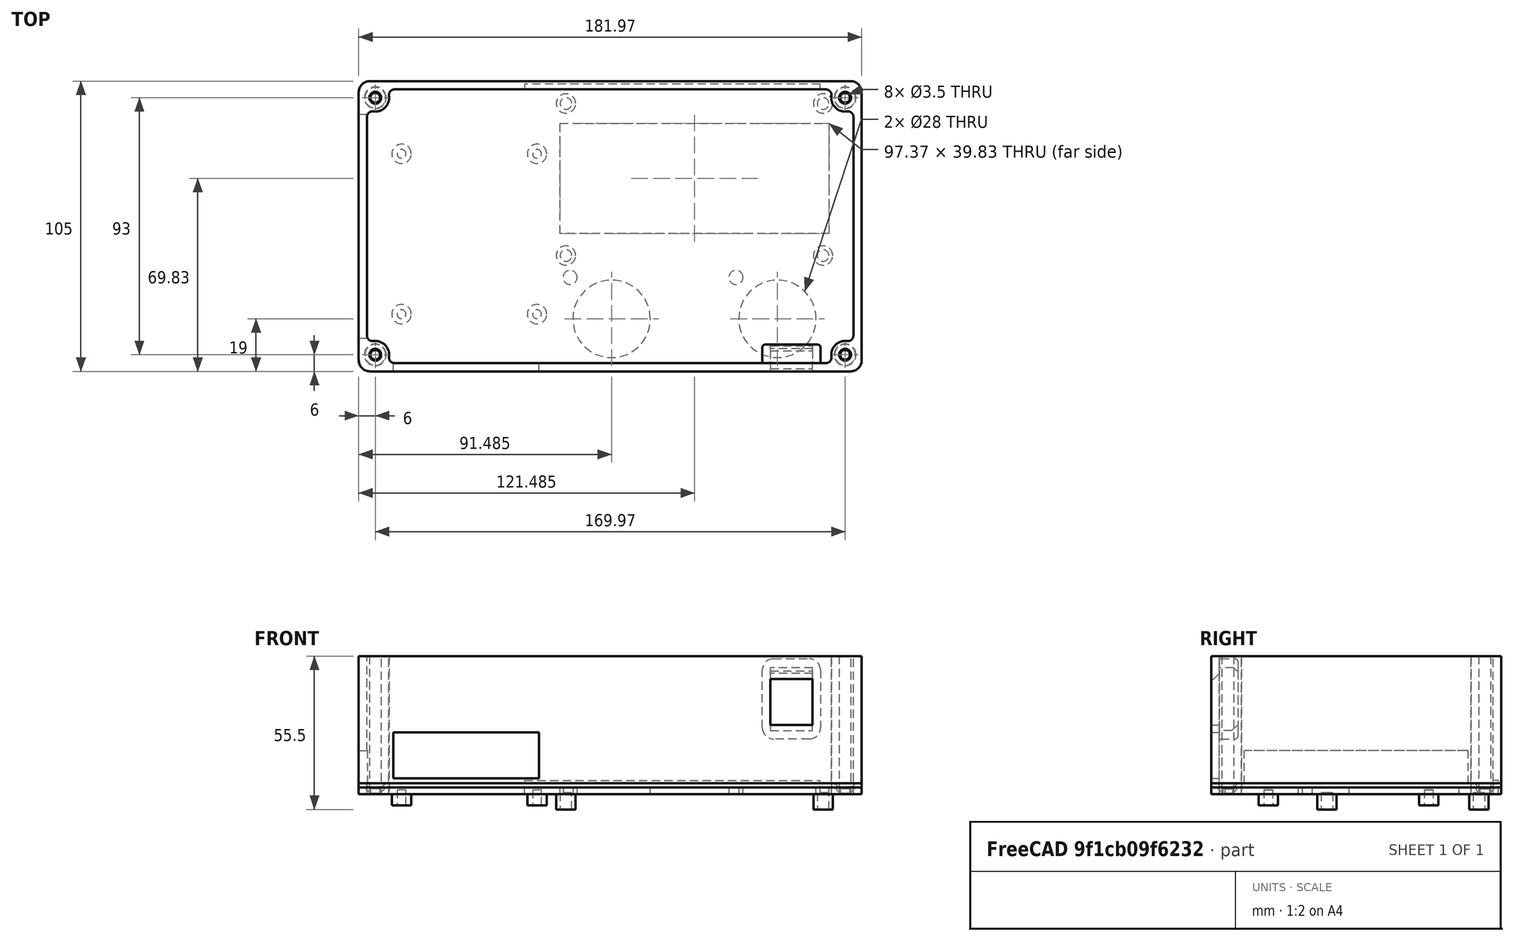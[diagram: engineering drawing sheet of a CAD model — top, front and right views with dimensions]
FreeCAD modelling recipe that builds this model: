
FCSTD DOCUMENT  (FreeCAD 0.21R33668 +26 (Git))
Label: j2b controller
License: All rights reserved
LicenseURL: https://en.wikipedia.org/wiki/All_rights_reserved
objects: Sketcher::SketchObject×13, PartDesign::Pocket×7, PartDesign::Pad×6, PartDesign::Fillet×5, PartDesign::Body×4, PartDesign::Chamfer×2, Part::Feature×2, Part::Refine×2, App::Part×2, Mesh::Feature×1, Part::Cut×1, PartDesign::FeatureBase×1
note: 63 computed .brp shape members not serialized (recipe doc carries the construction recipe); baked Part::Feature solids carry a one-line shape summary decoded from their .brp

FEATURE [Sketcher::SketchObject] Sketch
  FullyConstrained = false
  MapMode = 5
  Support = -> [XY_Plane001]
  sketch-geometry (42):
    g0: LineSegment StartX=0 StartY=0 StartZ=0 EndX=181.97 EndY=0 EndZ=0
    g1: LineSegment StartX=181.97 StartY=0 StartZ=0 EndX=181.97 EndY=-105 EndZ=0
    g2: LineSegment StartX=181.97 StartY=-105 StartZ=0 EndX=0 EndY=-105 EndZ=0
    g3: LineSegment StartX=0 StartY=-105 StartZ=0 EndX=0 EndY=0 EndZ=0
    g4: LineSegment StartX=12 StartY=-5 StartZ=0 EndX=68 EndY=-5 EndZ=0
    g5: LineSegment StartX=68 StartY=-5 StartZ=0 EndX=68 EndY=-90 EndZ=0
    g6: LineSegment StartX=68 StartY=-90 StartZ=0 EndX=12 EndY=-90 EndZ=0
    g7: LineSegment StartX=12 StartY=-90 StartZ=0 EndX=12 EndY=-5 EndZ=0
    g8: LineSegment StartX=73 StartY=-15.455 StartZ=0 EndX=169.97 EndY=-15.455 EndZ=0
    g9: LineSegment StartX=169.97 StartY=-15.455 StartZ=0 EndX=169.97 EndY=-54.885 EndZ=0
    g10: LineSegment StartX=169.97 StartY=-54.885 StartZ=0 EndX=73 EndY=-54.885 EndZ=0
    g11: LineSegment StartX=73 StartY=-54.885 StartZ=0 EndX=73 EndY=-15.455 EndZ=0
    g12: Circle CenterX=91.485 CenterY=-86 CenterZ=0 NormalX=0 NormalY=0 NormalZ=1 AngleXU=0 Radius=14
    g13: Circle CenterX=151.485 CenterY=-86 CenterZ=0 NormalX=0 NormalY=0 NormalZ=1 AngleXU=0 Radius=14
    g14: LineSegment StartX=91.485 StartY=-86 StartZ=0 EndX=151.485 EndY=-86 EndZ=0
    g15: LineSegment StartX=91.485 StartY=-86 StartZ=0 EndX=73 EndY=-54.885 EndZ=0
    g16: LineSegment StartX=151.485 StartY=-86 StartZ=0 EndX=169.97 EndY=-54.885 EndZ=0
    g17: LineSegment StartX=72.2333 StartY=-5 StartZ=0 EndX=170.737 EndY=-5 EndZ=0
    g18: LineSegment StartX=170.737 StartY=-5 StartZ=0 EndX=170.737 EndY=-65.34 EndZ=0
    g19: LineSegment StartX=170.737 StartY=-65.34 StartZ=0 EndX=72.2333 EndY=-65.34 EndZ=0
    g20: LineSegment StartX=72.2333 StartY=-65.34 StartZ=0 EndX=72.2333 EndY=-5 EndZ=0
    g21: LineSegment StartX=73 StartY=-15.455 StartZ=0 EndX=72.2333 EndY=-5 EndZ=0
    g22: LineSegment StartX=72.2333 StartY=-65.34 StartZ=0 EndX=73 EndY=-54.885 EndZ=0
    g23: LineSegment StartX=72.8 StartY=-15.255 StartZ=0 EndX=170.17 EndY=-15.255 EndZ=0
    g24: LineSegment StartX=170.17 StartY=-15.255 StartZ=0 EndX=170.17 EndY=-55.085 EndZ=0
    g25: LineSegment StartX=170.17 StartY=-55.085 StartZ=0 EndX=72.8 EndY=-55.085 EndZ=0
    g26: LineSegment StartX=72.8 StartY=-55.085 StartZ=0 EndX=72.8 EndY=-15.255 EndZ=0
    g27: Circle CenterX=136.485 CenterY=-71 CenterZ=0 NormalX=0 NormalY=0 NormalZ=1 AngleXU=0 Radius=2.55
    g28: LineSegment StartX=151.485 StartY=-86 StartZ=0 EndX=136.485 EndY=-86 EndZ=0
    g29: LineSegment StartX=136.485 StartY=-86 StartZ=0 EndX=136.485 EndY=-71 EndZ=0
    g30: LineSegment StartX=136.485 StartY=-71 StartZ=0 EndX=151.485 EndY=-71 EndZ=0
    g31: LineSegment StartX=151.485 StartY=-71 StartZ=0 EndX=151.485 EndY=-86 EndZ=0
    g32: Circle CenterX=76.485 CenterY=-71 CenterZ=0 NormalX=0 NormalY=0 NormalZ=1 AngleXU=0 Radius=2.55
    g33: LineSegment StartX=76.485 StartY=-71 StartZ=0 EndX=91.485 EndY=-71 EndZ=0
    g34: LineSegment StartX=91.485 StartY=-71 StartZ=0 EndX=91.485 EndY=-86 EndZ=0
    g35: LineSegment StartX=91.485 StartY=-86 StartZ=0 EndX=76.485 EndY=-86 EndZ=0
    g36: LineSegment StartX=76.485 StartY=-86 StartZ=0 EndX=76.485 EndY=-71 EndZ=0
    g37: LineSegment StartX=169.97 StartY=-15.455 StartZ=0 EndX=170.737 EndY=-5 EndZ=0
    g38: Circle CenterX=6 CenterY=-99 CenterZ=0 NormalX=0 NormalY=0 NormalZ=1 AngleXU=0 Radius=1.75
    g39: Circle CenterX=175.97 CenterY=-99 CenterZ=0 NormalX=0 NormalY=0 NormalZ=1 AngleXU=0 Radius=1.75
    g40: Circle CenterX=6 CenterY=-6 CenterZ=0 NormalX=0 NormalY=0 NormalZ=1 AngleXU=0 Radius=1.75
    g41: Circle CenterX=175.97 CenterY=-6 CenterZ=0 NormalX=0 NormalY=0 NormalZ=1 AngleXU=0 Radius=1.75
  constraints (114):
    c: Coincident(g0,g1)
    c: Coincident(g1,g2)
    c: Coincident(g2,g3)
    c: Coincident(g3,g0)
    c: Horizontal(g0)
    c: Horizontal(g2)
    c: Vertical(g1)
    c: Vertical(g3)
    c: Coincident(g0,g-1)
    c: Coincident(g4,g5)
    c: Coincident(g5,g6)
    c: Coincident(g6,g7)
    c: Coincident(g7,g4)
    c: Horizontal(g4)
    c: Horizontal(g6)
    c: Vertical(g5)
    c: Vertical(g7)
    c: DistanceX(g4,g4) = 56
    c: DistanceY(g5,g5) = 85
    c: DistanceX(g0,g4) = 12
    c: DistanceY(g4,g0) = 5
    c: DistanceY(g2,g6) = 15
    c: Coincident(g8,g9)
    c: Coincident(g9,g10)
    c: Coincident(g10,g11)
    c: Coincident(g11,g8)
    c: Horizontal(g8)
    c: Horizontal(g10)
    c: Vertical(g9)
    c: Vertical(g11)
    c: DistanceX(g8,g8) = 96.97
    c: DistanceY(g11,g11) = 39.43
    c: Diameter(g12) = 28
    c: Equal(g12,g13)
    c: Coincident(g14,g12)
    c: Coincident(g14,g13)
    c: Horizontal(g14)
    c: Coincident(g15,g12)
    c: Coincident(g15,g10)
    c: Coincident(g16,g13)
    c: Coincident(g16,g9)
    c: Equal(g15,g16)
    c: DistanceX(g14,g14) = 60
    c: DistanceX(g8,g0) = 12
    c: DistanceX(g4,g8) = 5
    c: Coincident(g17,g18)
    c: Coincident(g18,g19)
    c: Coincident(g19,g20)
    c: Coincident(g20,g17)
    c: Horizontal(g17)
    c: Horizontal(g19)
    c: Vertical(g18)
    c: Vertical(g20)
    c: DistanceY(g18,g18) = 60.34
    c: Coincident(g21,g8)
    c: Coincident(g21,g17)
    c: Coincident(g22,g19)
    c: Coincident(g22,g10)
    c: Equal(g22,g21)
    c: DistanceY(g17,g0) = 5
    c: DistanceY(g1,g13) = 19
    c: Coincident(g23,g24)
    c: Coincident(g24,g25)
    c: Coincident(g25,g26)
    c: Coincident(g26,g23)
    c: Horizontal(g23)
    c: Horizontal(g25)
    c: Vertical(g24)
    c: Vertical(g26)
    c: DistanceY(g8,g23) = 0.2
    c: DistanceY(g24,g9) = 0.2
    c: DistanceX(g23,g8) = 0.2
    c: DistanceX(g8,g23) = 0.2
    c: Diameter(g27) = 5.1
    c: Coincident(g28,g29)
    c: Coincident(g29,g30)
    c: Coincident(g30,g31)
    c: Coincident(g31,g28)
    c: Horizontal(g28)
    c: Horizontal(g30)
    c: Vertical(g29)
    c: Vertical(g31)
    c: Coincident(g28,g13)
    c: Coincident(g29,g27)
    c: Equal(g29,g30)
    c: DistanceY(g29,g29) = 15
    c: Coincident(g33,g34)
    c: Coincident(g34,g35)
    c: Coincident(g35,g36)
    c: Coincident(g36,g33)
    c: Horizontal(g33)
    c: Horizontal(g35)
    c: Vertical(g34)
    c: Vertical(g36)
    c: Coincident(g33,g32)
    c: Coincident(g34,g12)
    c: Equal(g36,g33)
    c: Equal(g33,g30)
    c: Equal(g27,g32)
    c: Coincident(g37,g8)
    c: Coincident(g37,g17)
    c: Equal(g21,g37)
    c: Diameter(g40) = 3.5
    c: Diameter(g38) = 3.5
    c: Diameter(g39) = 3.5
    c: Diameter(g41) = 3.5
    c: Vertical(g38,g40)
    c: Vertical(g41,g39)
    c: DistanceX(g0,g40) = 6
    c: Horizontal(g40,g41)
    c: Horizontal(g39,g38)
    c: DistanceY(g40,g0) = 6
    c: DistanceY(g2,g38) = 6
    c: DistanceX(g41,g0) = 6
FEATURE [PartDesign::Pad] Pad
  Direction = (0,0,1)
  Length = 2.5
  Length2 = 10
  Profile = -> Sketch
  ReferenceAxis = -> Sketch [N_Axis]
  Type = 0
FEATURE [PartDesign::Chamfer] Chamfer
  Angle = 45
  Base = -> Pad [Edge42,Edge48,Edge45,Edge39]
  BaseFeature = -> Pad
  ChamferType = 0
  FlipDirection = false
  Size = 2.2
  Size2 = 1
  SupportTransform = false
  UseAllEdges = false
FEATURE [Sketcher::SketchObject] Sketch001
  ExternalGeometry = -> [Chamfer]
  FullyConstrained = true
  MapMode = 5
  Placement = pos=(0,0,0) rot=(1,0,0;3.14159rad)
  Support = -> [Chamfer]
  sketch-geometry (14):
    g0: LineSegment StartX=12 StartY=87.8 StartZ=0 EndX=68 EndY=87.8 EndZ=0
    g1: LineSegment StartX=68 StartY=87.8 StartZ=0 EndX=68 EndY=2.8 EndZ=0
    g2: LineSegment StartX=68 StartY=2.8 StartZ=0 EndX=12 EndY=2.8 EndZ=0
    g3: LineSegment StartX=12 StartY=2.8 StartZ=0 EndX=12 EndY=87.8 EndZ=0
    g4: LineSegment StartX=15.5 StartY=84.3 StartZ=0 EndX=64.5 EndY=84.3 EndZ=0
    g5: LineSegment StartX=64.5 StartY=84.3 StartZ=0 EndX=64.5 EndY=26.3 EndZ=0
    g6: LineSegment StartX=64.5 StartY=26.3 StartZ=0 EndX=15.5 EndY=26.3 EndZ=0
    g7: LineSegment StartX=15.5 StartY=26.3 StartZ=0 EndX=15.5 EndY=84.3 EndZ=0
    g8: LineSegment StartX=15.5 StartY=84.3 StartZ=0 EndX=12 EndY=87.8 EndZ=0
    g9: LineSegment StartX=64.5 StartY=84.3 StartZ=0 EndX=68 EndY=87.8 EndZ=0
    g10: Circle CenterX=15.5 CenterY=84.3 CenterZ=0 NormalX=0 NormalY=0 NormalZ=1 AngleXU=0 Radius=3.5
    g11: Circle CenterX=64.5 CenterY=84.3 CenterZ=0 NormalX=0 NormalY=0 NormalZ=1 AngleXU=0 Radius=3.5
    g12: Circle CenterX=64.5 CenterY=26.3 CenterZ=0 NormalX=0 NormalY=0 NormalZ=1 AngleXU=0 Radius=3.5
    g13: Circle CenterX=15.5 CenterY=26.3 CenterZ=0 NormalX=0 NormalY=0 NormalZ=1 AngleXU=0 Radius=3.5
  constraints (36):
    c: Coincident(g0,g1)
    c: Coincident(g1,g2)
    c: Coincident(g2,g3)
    c: Coincident(g3,g0)
    c: Horizontal(g0)
    c: Horizontal(g2)
    c: Vertical(g1)
    c: Vertical(g3)
    c: Coincident(g4,g5)
    c: Coincident(g5,g6)
    c: Coincident(g6,g7)
    c: Coincident(g7,g4)
    c: Horizontal(g4)
    c: Horizontal(g6)
    c: Vertical(g5)
    c: Vertical(g7)
    c: DistanceX(g2,g2) = 56
    c: DistanceX(g6,g6) = 49
    c: DistanceY(g3,g3) = 85
    c: DistanceY(g7,g7) = 58
    c: DistanceY(g4,g0) = 3.5
    c: Coincident(g8,g4)
    c: Coincident(g8,g0)
    c: Coincident(g9,g4)
    c: Coincident(g9,g0)
    c: Equal(g8,g9)
    c: DistanceX(g-5,g0) = 12
    c: DistanceY(g-4,g2) = 2.8
    c: Coincident(g10,g4)
    c: Coincident(g11,g4)
    c: Coincident(g12,g5)
    c: Coincident(g13,g6)
    c: Equal(g10,g11)
    c: Equal(g11,g12)
    c: Equal(g12,g13)
    c: Diameter(g10) = 7
FEATURE [PartDesign::Pad] Pad001
  BaseFeature = -> Chamfer
  Direction = (0,0,-1)
  Length = 4
  Length2 = 10
  Profile = -> Sketch001
  ReferenceAxis = -> Sketch001 [N_Axis]
  Type = 0
FEATURE [Sketcher::SketchObject] Sketch002
  ExternalGeometry = -> [Pad001]
  FullyConstrained = true
  MapMode = 5
  Placement = pos=(0,0,0) rot=(1,0,0;3.14159rad)
  Support = -> [Pad001]
  sketch-geometry (10):
    g0: LineSegment StartX=74.985 StartY=63.085 StartZ=0 EndX=167.985 EndY=63.085 EndZ=0
    g1: LineSegment StartX=167.985 StartY=63.085 StartZ=0 EndX=167.985 EndY=8.085 EndZ=0
    g2: LineSegment StartX=167.985 StartY=8.085 StartZ=0 EndX=74.985 EndY=8.085 EndZ=0
    g3: LineSegment StartX=74.985 StartY=8.085 StartZ=0 EndX=74.985 EndY=63.085 EndZ=0
    g4: Circle CenterX=74.985 CenterY=63.085 CenterZ=0 NormalX=0 NormalY=0 NormalZ=1 AngleXU=0 Radius=3.5
    g5: Circle CenterX=167.985 CenterY=63.085 CenterZ=0 NormalX=0 NormalY=0 NormalZ=1 AngleXU=0 Radius=3.5
    g6: Circle CenterX=167.985 CenterY=8.085 CenterZ=0 NormalX=0 NormalY=0 NormalZ=1 AngleXU=0 Radius=3.5
    g7: Circle CenterX=74.985 CenterY=8.085 CenterZ=0 NormalX=0 NormalY=0 NormalZ=1 AngleXU=0 Radius=3.5
    g8: LineSegment StartX=72.8 StartY=15.255 StartZ=0 EndX=74.985 EndY=8.085 EndZ=0
    g9: LineSegment StartX=167.985 StartY=8.085 StartZ=0 EndX=170.17 EndY=15.255 EndZ=0
  constraints (24):
    c: Coincident(g0,g1)
    c: Coincident(g1,g2)
    c: Coincident(g2,g3)
    c: Coincident(g3,g0)
    c: Horizontal(g0)
    c: Horizontal(g2)
    c: Vertical(g1)
    c: Vertical(g3)
    c: DistanceY(g1,g1) = 55
    c: DistanceX(g0,g0) = 93
    c: Coincident(g4,g0)
    c: Coincident(g5,g0)
    c: Coincident(g6,g1)
    c: Coincident(g7,g2)
    c: Equal(g4,g7)
    c: Equal(g6,g7)
    c: Equal(g6,g5)
    c: Diameter(g4) = 7
    c: DistanceY(g-3,g5) = 8
    c: Coincident(g8,g-4)
    c: Coincident(g8,g7)
    c: Coincident(g9,g6)
    c: Coincident(g9,g-4)
    c: Equal(g8,g9)
FEATURE [PartDesign::Pad] Pad002
  BaseFeature = -> Pad001
  Direction = (0,0,-1)
  Length = 5.5
  Length2 = 10
  Profile = -> Sketch002
  ReferenceAxis = -> Sketch002 [N_Axis]
  Type = 0
FEATURE [Sketcher::SketchObject] Sketch003
  ExternalGeometry = -> [Pad002]
  FullyConstrained = true
  MapMode = 5
  Placement = pos=(0,0,-5.5) rot=(1,0,0;3.14159rad)
  Support = -> [Pad002]
  sketch-geometry (4):
    g0: Circle CenterX=74.985 CenterY=63.085 CenterZ=0 NormalX=0 NormalY=0 NormalZ=1 AngleXU=0 Radius=2.1
    g1: Circle CenterX=167.985 CenterY=63.085 CenterZ=0 NormalX=0 NormalY=0 NormalZ=1 AngleXU=0 Radius=2.1
    g2: Circle CenterX=167.985 CenterY=8.085 CenterZ=0 NormalX=0 NormalY=0 NormalZ=1 AngleXU=0 Radius=2.1
    g3: Circle CenterX=74.985 CenterY=8.085 CenterZ=0 NormalX=0 NormalY=0 NormalZ=1 AngleXU=0 Radius=2.1
  constraints (8):
    c: Coincident(g0,g-3)
    c: Coincident(g1,g-4)
    c: Coincident(g2,g-6)
    c: Coincident(g3,g-5)
    c: Equal(g0,g1)
    c: Equal(g1,g2)
    c: Equal(g2,g3)
    c: Diameter(g0) = 4.2
FEATURE [PartDesign::Pocket] Pocket
  BaseFeature = -> Pad002
  Direction = (0,0,1)
  Length = 6
  Length2 = 5
  Profile = -> Sketch003
  ReferenceAxis = -> Sketch003 [N_Axis]
  Type = 0
FEATURE [Sketcher::SketchObject] Sketch004
  ExternalGeometry = -> [Pocket]
  FullyConstrained = true
  MapMode = 5
  Placement = pos=(0,0,-4) rot=(1,0,0;3.14159rad)
  Support = -> [Pocket]
  sketch-geometry (4):
    g0: Circle CenterX=15.5 CenterY=84.3 CenterZ=0 NormalX=0 NormalY=0 NormalZ=1 AngleXU=0 Radius=1.6
    g1: Circle CenterX=64.5 CenterY=84.3 CenterZ=0 NormalX=0 NormalY=0 NormalZ=1 AngleXU=0 Radius=1.6
    g2: Circle CenterX=64.5 CenterY=26.3 CenterZ=0 NormalX=0 NormalY=0 NormalZ=1 AngleXU=0 Radius=1.6
    g3: Circle CenterX=15.5 CenterY=26.3 CenterZ=0 NormalX=0 NormalY=0 NormalZ=1 AngleXU=0 Radius=1.6
  constraints (8):
    c: Coincident(g0,g-3)
    c: Coincident(g1,g-4)
    c: Coincident(g3,g-5)
    c: Equal(g0,g1)
    c: Equal(g1,g2)
    c: Equal(g2,g3)
    c: Diameter(g0) = 3.2
    c: Coincident(g2,g-6)
FEATURE [PartDesign::Pocket] Pocket001
  BaseFeature = -> Pocket
  Direction = (0,0,1)
  Length = 5.5
  Length2 = 5
  Profile = -> Sketch004
  ReferenceAxis = -> Sketch004 [N_Axis]
  Type = 0
FEATURE [PartDesign::Fillet] Fillet
  Base = -> Pocket001 [Edge44,Edge46,Edge45,Edge47]
  BaseFeature = -> Pocket001
  Radius = 4
  SupportTransform = false
  UseAllEdges = false
FEATURE [PartDesign::Body] Body
  Group = -> [Sketch,Pad,Chamfer,Sketch001,Pad001,Sketch002,Pad002,Sketch003,Pocket,Sketch004,Pocket001,Fillet]
  Origin = -> Origin001
  Tip = -> Fillet
FEATURE [PartDesign::Body] Body001
  Origin = -> Origin002
FEATURE [Sketcher::SketchObject] Sketch005
  FullyConstrained = true
  MapMode = 5
  Support = -> [XY_Plane002]
  sketch-geometry (16):
    g0: LineSegment StartX=4 StartY=0 StartZ=0 EndX=177.97 EndY=0 EndZ=0
    g1: LineSegment StartX=181.97 StartY=-4 StartZ=0 EndX=181.97 EndY=-101 EndZ=0
    g2: LineSegment StartX=177.97 StartY=-105 StartZ=0 EndX=4 EndY=-105 EndZ=0
    g3: LineSegment StartX=0 StartY=-101 StartZ=0 EndX=0 EndY=-4 EndZ=0
    g4: ArcOfCircle CenterX=4 CenterY=-4 CenterZ=0 NormalX=0 NormalY=0 NormalZ=1 AngleXU=0 Radius=4 StartAngle=1.5708 EndAngle=3.14159
    g5: ArcOfCircle CenterX=177.97 CenterY=-4 CenterZ=0 NormalX=0 NormalY=0 NormalZ=1 AngleXU=0 Radius=4 StartAngle=0 EndAngle=1.5708
    g6: ArcOfCircle CenterX=177.97 CenterY=-101 CenterZ=0 NormalX=0 NormalY=0 NormalZ=1 AngleXU=0 Radius=4 StartAngle=4.71239 EndAngle=6.28319
    g7: ArcOfCircle CenterX=4 CenterY=-101 CenterZ=0 NormalX=0 NormalY=0 NormalZ=1 AngleXU=0 Radius=4 StartAngle=3.14159 EndAngle=4.71239
    g8: LineSegment StartX=10 StartY=-3 StartZ=0 EndX=171.97 EndY=-3 EndZ=0
    g9: LineSegment StartX=178.97 StartY=-10 StartZ=0 EndX=178.97 EndY=-95 EndZ=0
    g10: LineSegment StartX=171.97 StartY=-102 StartZ=0 EndX=10 EndY=-102 EndZ=0
    g11: LineSegment StartX=3 StartY=-95 StartZ=0 EndX=3 EndY=-10 EndZ=0
    g12: ArcOfCircle CenterX=6 CenterY=-6 CenterZ=0 NormalX=0 NormalY=0 NormalZ=1 AngleXU=0 Radius=5 StartAngle=4.06889 EndAngle=6.92669
    g13: ArcOfCircle CenterX=175.97 CenterY=-6 CenterZ=0 NormalX=0 NormalY=0 NormalZ=1 AngleXU=0 Radius=5 StartAngle=2.49809 EndAngle=5.35589
    g14: ArcOfCircle CenterX=175.97 CenterY=-99 CenterZ=0 NormalX=0 NormalY=0 NormalZ=1 AngleXU=0 Radius=5 StartAngle=0.927295 EndAngle=3.78509
    g15: ArcOfCircle CenterX=6 CenterY=-99 CenterZ=0 NormalX=0 NormalY=0 NormalZ=1 AngleXU=0 Radius=5 StartAngle=5.63968 EndAngle=8.49748
  constraints (48):
    c: Horizontal(g0)
    c: Horizontal(g2)
    c: Vertical(g1)
    c: Vertical(g3)
    c: Tangent(g3,g4) = 1.5708
    c: Tangent(g0,g4) = 1.5708
    c: Tangent(g0,g5) = 1.5708
    c: Tangent(g1,g5) = 1.5708
    c: Tangent(g1,g6) = 1.5708
    c: Tangent(g2,g6) = 1.5708
    c: Tangent(g2,g7) = 1.5708
    c: Tangent(g3,g7) = 1.5708
    c: Diameter(g4) = 8
    c: Equal(g4,g5)
    c: Equal(g5,g6)
    c: Equal(g6,g7)
    c: DistanceX(g3,g1) = 181.97
    c: DistanceY(g2,g0) = 105
    c: Horizontal(g0,g-1)
    c: Vertical(g3,g-1)
    c: Horizontal(g8)
    c: Vertical(g9)
    c: Horizontal(g10)
    c: Vertical(g11)
    c: Coincident(g12,g8)
    c: Coincident(g11,g12)
    c: DistanceX(g-1,g12) = 6
    c: DistanceY(g12,g-1) = 6
    c: Diameter(g12) = 10
    c: DistanceX(g3,g11) = 3
    c: DistanceY(g8,g0) = 3
    c: Coincident(g13,g8)
    c: Coincident(g13,g9)
    c: Coincident(g14,g9)
    c: Coincident(g14,g10)
    c: Coincident(g15,g11)
    c: Coincident(g15,g10)
    c: Diameter(g13) = 10
    c: Diameter(g15) = 10
    c: Diameter(g14) = 10
    c: Vertical(g15,g12)
    c: Horizontal(g15,g14)
    c: Vertical(g13,g14)
    c: DistanceY(g2,g10) = 3
    c: DistanceX(g9,g1) = 3
    c: DistanceX(g13,g1) = 6
    c: DistanceY(g2,g15) = 6
    c: DistanceY(g13,g0) = 6
FEATURE [PartDesign::Pad] Pad003
  Direction = (0,0,1)
  Length = 50
  Length2 = 10
  Profile = -> Sketch005
  ReferenceAxis = -> Sketch005 [N_Axis]
  Type = 0
FEATURE [Sketcher::SketchObject] Sketch006
  ExternalGeometry = -> [Pad003]
  FullyConstrained = true
  MapMode = 5
  Placement = pos=(0,0,0) rot=(1,0,0;3.14159rad)
  Support = -> [Pad003]
  sketch-geometry (4):
    g0: LineSegment StartX=60 StartY=3 StartZ=0 EndX=166.97 EndY=3 EndZ=0
    g1: LineSegment StartX=166.97 StartY=3 StartZ=0 EndX=166.97 EndY=1 EndZ=0
    g2: LineSegment StartX=166.97 StartY=1 StartZ=0 EndX=60 EndY=1 EndZ=0
    g3: LineSegment StartX=60 StartY=1 StartZ=0 EndX=60 EndY=3 EndZ=0
  constraints (12):
    c: Coincident(g0,g1)
    c: Coincident(g1,g2)
    c: Coincident(g2,g3)
    c: Coincident(g3,g0)
    c: Horizontal(g0)
    c: Horizontal(g2)
    c: Vertical(g1)
    c: Vertical(g3)
    c: PointOnObject(g0,g-3)
    c: DistanceY(g-4,g1) = 1
    c: DistanceX(g0,g-5) = 15
    c: DistanceX(g-7,g0) = 60
FEATURE [PartDesign::Pocket] Pocket002
  Direction = (0,0,1)
  Length = 5
  Length2 = 5
  Profile = -> Sketch006
  ReferenceAxis = -> Sketch006 [N_Axis]
  Type = 0
FEATURE [Sketcher::SketchObject] Sketch007
  ExternalGeometry = -> [Pocket002]
  FullyConstrained = true
  MapMode = 5
  Placement = pos=(0,0,0) rot=(1,0,0;3.14159rad)
  Support = -> [Pocket002]
  sketch-geometry (4):
    g0: Circle CenterX=6 CenterY=99 CenterZ=0 NormalX=0 NormalY=0 NormalZ=1 AngleXU=0 Radius=2.15
    g1: Circle CenterX=175.97 CenterY=99 CenterZ=0 NormalX=0 NormalY=0 NormalZ=1 AngleXU=0 Radius=2.15
    g2: Circle CenterX=6 CenterY=6 CenterZ=0 NormalX=0 NormalY=0 NormalZ=1 AngleXU=0 Radius=2.15
    g3: Circle CenterX=175.97 CenterY=6 CenterZ=0 NormalX=0 NormalY=0 NormalZ=1 AngleXU=0 Radius=2.15
  constraints (8):
    c: Coincident(g0,g-3)
    c: Coincident(g1,g-4)
    c: Coincident(g2,g-6)
    c: Coincident(g3,g-5)
    c: Diameter(g0) = 4.3
    c: Diameter(g1) = 4.3
    c: Diameter(g2) = 4.3
    c: Diameter(g3) = 4.3
FEATURE [PartDesign::Pocket] Pocket003
  Direction = (0,0,1)
  Length = 5
  Length2 = 5
  Profile = -> Sketch007
  ReferenceAxis = -> Sketch007 [N_Axis]
  Type = 1
FEATURE [PartDesign::Fillet] Fillet001
  Base = -> Pocket003 [Edge58,Edge63,Edge56,Edge57,Edge66,Edge69,Edge71,Edge62]
  Radius = 2
  SupportTransform = false
  UseAllEdges = false
FEATURE [Sketcher::SketchObject] Sketch008
  FullyConstrained = true
  MapMode = 5
  Placement = pos=(0,-105,0) rot=(1,0,0;1.5708rad)
  Support = -> [Fillet001]
  sketch-geometry (4):
    g0: LineSegment StartX=12.5 StartY=5.8 StartZ=0 EndX=65.2 EndY=5.8 EndZ=0
    g1: LineSegment StartX=65.2 StartY=5.8 StartZ=0 EndX=65.2 EndY=22.4 EndZ=0
    g2: LineSegment StartX=65.2 StartY=22.4 StartZ=0 EndX=12.5 EndY=22.4 EndZ=0
    g3: LineSegment StartX=12.5 StartY=22.4 StartZ=0 EndX=12.5 EndY=5.8 EndZ=0
  constraints (12):
    c: Coincident(g0,g1)
    c: Coincident(g1,g2)
    c: Coincident(g2,g3)
    c: Coincident(g3,g0)
    c: Horizontal(g0)
    c: Horizontal(g2)
    c: Vertical(g1)
    c: Vertical(g3)
    c: DistanceX(g-1,g0) = 12.5
    c: DistanceX(g-1,g0) = 65.2
    c: DistanceY(g-1,g0) = 5.8
    c: DistanceY(g-1,g2) = 22.4
FEATURE [PartDesign::Pocket] Pocket004
  Direction = (0,1,-2e-16)
  Length = 5
  Length2 = 5
  Profile = -> Sketch008
  ReferenceAxis = -> Sketch008 [N_Axis]
  Type = 0
FEATURE [Sketcher::SketchObject] Sketch009
  ExternalGeometry = -> [Pocket004]
  FullyConstrained = true
  MapMode = 5
  Placement = pos=(0,0,0) rot=(0.57735,-0.57735,-0.57735;2.0944rad)
  Support = -> [Pocket004]
  sketch-geometry (4):
    g0: LineSegment StartX=79 StartY=3.5 StartZ=0 EndX=20 EndY=3.5 EndZ=0
    g1: LineSegment StartX=20 StartY=3.5 StartZ=0 EndX=20 EndY=13 EndZ=0
    g2: LineSegment StartX=20 StartY=13 StartZ=0 EndX=79 EndY=13 EndZ=0
    g3: LineSegment StartX=79 StartY=13 StartZ=0 EndX=79 EndY=3.5 EndZ=0
  constraints (12):
    c: Coincident(g0,g1)
    c: Coincident(g1,g2)
    c: Coincident(g2,g3)
    c: Coincident(g3,g0)
    c: Horizontal(g0)
    c: Horizontal(g2)
    c: Vertical(g1)
    c: Vertical(g3)
    c: DistanceX(g-1,g0) = 20
    c: DistanceX(g0,g-3) = 26
    c: DistanceY(g-1,g0) = 3.5
    c: DistanceY(g-1,g1) = 13
FEATURE [PartDesign::Pocket] Pocket005
  BaseFeature = -> Pocket004
  Direction = (1,0,0)
  Length = 5
  Length2 = 5
  Profile = -> Sketch009
  ReferenceAxis = -> Sketch009 [N_Axis]
  Type = 0
FEATURE [Mesh::Feature] Keystone_Jack_negative_Space
FEATURE [Part::Feature] Keystone_Jack_negative_Space001
  shape: bbox 15.2 x 9.8 x 22.7 mm, 48 faces, 0 solids (baked)
FEATURE [Part::Feature] Keystone_Jack_negative_Space001_solid  label="Keystone_Jack_negative_Space001 (Solid)"
  shape: bbox 15.2 x 9.8 x 22.7 mm, 48 faces (baked)
FEATURE [Part::Refine] Keystone_Jack_negative_Space001_solid001  label="Keystone Jack"
  Placement = pos=(160,-97.365,23) rot=(0,0,1;0rad)
  Source = -> Keystone_Jack_negative_Space001_solid
FEATURE [Sketcher::SketchObject] Sketch010
  ExternalGeometry = -> [Pocket005]
  FullyConstrained = true
  MapMode = 5
  Placement = pos=(0,-102,0) rot=(0,0.707107,0.707107;3.14159rad)
  Support = -> [Pocket005]
  sketch-geometry (4):
    g0: LineSegment StartX=-167.042 StartY=20 StartZ=0 EndX=-146.042 EndY=20 EndZ=0
    g1: LineSegment StartX=-146.042 StartY=20 StartZ=0 EndX=-146.042 EndY=49 EndZ=0
    g2: LineSegment StartX=-146.042 StartY=49 StartZ=0 EndX=-167.042 EndY=49 EndZ=0
    g3: LineSegment StartX=-167.042 StartY=49 StartZ=0 EndX=-167.042 EndY=20 EndZ=0
  constraints (12):
    c: Coincident(g0,g1)
    c: Coincident(g1,g2)
    c: Coincident(g2,g3)
    c: Coincident(g3,g0)
    c: Horizontal(g0)
    c: Horizontal(g2)
    c: Vertical(g1)
    c: Vertical(g3)
    c: DistanceX(g-3,g2) = 2
    c: DistanceX(g-3,g1) = 23
    c: DistanceY(g2,g-3) = 1
    c: DistanceY(g0,g-3) = 30
FEATURE [PartDesign::Pad] Pad004
  BaseFeature = -> Pocket004
  Direction = (0,1,-2e-16)
  Length = 6.7
  Length2 = 10
  Profile = -> Sketch010
  ReferenceAxis = -> Sketch010 [N_Axis]
  Type = 0
FEATURE [Part::Refine] Pad005  label="Sides"
  Source = -> Pad004
FEATURE [Part::Cut] Cut001
  Base = -> Pad005
  Tool = -> Keystone_Jack_negative_Space001_solid001
FEATURE [PartDesign::FeatureBase] BaseFeature
  BaseFeature = -> Cut001
FEATURE [PartDesign::Fillet] Fillet002
  Base = -> BaseFeature [Edge121,Edge125,Edge123,Edge120]
  BaseFeature = -> BaseFeature
  Radius = 4
  SupportTransform = false
  UseAllEdges = false
FEATURE [PartDesign::Fillet] Fillet003
  Base = -> Fillet002 [Edge25]
  BaseFeature = -> Fillet002
  Radius = 1
  SupportTransform = false
  UseAllEdges = false
FEATURE [PartDesign::Fillet] Fillet004
  Base = -> Fillet003 [Edge12]
  BaseFeature = -> Fillet003
  Radius = 0.5
  SupportTransform = false
  UseAllEdges = false
FEATURE [Sketcher::SketchObject] Sketch011
  ExternalGeometry = -> [Fillet004]
  FullyConstrained = true
  MapMode = 5
  Placement = pos=(0,0,0) rot=(0.57735,-0.57735,-0.57735;2.0944rad)
  Support = -> [Fillet004]
  sketch-geometry (4):
    g0: LineSegment StartX=93 StartY=3.8 StartZ=0 EndX=12 EndY=3.8 EndZ=0
    g1: LineSegment StartX=12 StartY=3.8 StartZ=0 EndX=12 EndY=15.8 EndZ=0
    g2: LineSegment StartX=12 StartY=15.8 StartZ=0 EndX=93 EndY=15.8 EndZ=0
    g3: LineSegment StartX=93 StartY=15.8 StartZ=0 EndX=93 EndY=3.8 EndZ=0
  constraints (12):
    c: Coincident(g0,g1)
    c: Coincident(g1,g2)
    c: Coincident(g2,g3)
    c: Coincident(g3,g0)
    c: Horizontal(g0)
    c: Horizontal(g2)
    c: Vertical(g1)
    c: Vertical(g3)
    c: DistanceY(g3,g3) = 12
    c: DistanceY(g0,g-3) = 2
    c: DistanceX(g2,g-3) = 12
    c: DistanceX(g-1,g0) = 12
FEATURE [PartDesign::Pocket] Pocket006
  BaseFeature = -> Fillet004
  Direction = (1,0,0)
  Length = 5
  Length2 = 5
  Profile = -> Sketch011
  ReferenceAxis = -> Sketch011 [N_Axis]
  Type = 0
FEATURE [PartDesign::Body] Body002
  BaseFeature = -> Cut001
  Group = -> [BaseFeature,Fillet002,Fillet003,Fillet004,Sketch011,Pocket006]
  Origin = -> Origin003
  Tip = -> Pocket006
FEATURE [App::Part] Part
  Group = -> [Body,Body001,Pad003,Pocket002,Pocket003,Sketch010,Keystone_Jack_negative_Space001_solid,Fillet001,Cut001,Pad005,Sketch008,Pocket005,Pad004,Pocket004,Sketch006,Sketch007,Sketch005,Keystone_Jack_negative_Space001_solid001,Sketch009,Body002]
  Origin = -> Origin
FEATURE [Sketcher::SketchObject] Sketch012
  FullyConstrained = true
  MapMode = 5
  Support = -> [XY_Plane005]
  sketch-geometry (18):
    g0: ArcOfCircle CenterX=4 CenterY=-4 CenterZ=0 NormalX=0 NormalY=0 NormalZ=1 AngleXU=0 Radius=4 StartAngle=1.5708 EndAngle=3.14159
    g1: LineSegment StartX=4 StartY=-1.705e-13 StartZ=0 EndX=177.97 EndY=-1.705e-13 EndZ=0
    g2: ArcOfCircle CenterX=177.97 CenterY=-4 CenterZ=0 NormalX=0 NormalY=0 NormalZ=1 AngleXU=0 Radius=4 StartAngle=2e-16 EndAngle=1.5708
    g3: LineSegment StartX=181.97 StartY=-4 StartZ=0 EndX=181.97 EndY=-101 EndZ=0
    g4: ArcOfCircle CenterX=177.97 CenterY=-101 CenterZ=0 NormalX=0 NormalY=0 NormalZ=1 AngleXU=0 Radius=4 StartAngle=4.71239 EndAngle=6.28319
    g5: LineSegment StartX=177.97 StartY=-105 StartZ=0 EndX=4 EndY=-105 EndZ=0
    g6: ArcOfCircle CenterX=4 CenterY=-101 CenterZ=0 NormalX=0 NormalY=0 NormalZ=1 AngleXU=0 Radius=4 StartAngle=3.14159 EndAngle=4.71239
    g7: LineSegment StartX=0 StartY=-101 StartZ=0 EndX=0 EndY=-4 EndZ=0
    g8: GeomPoint X=0 Y=0 Z=0
    g9: GeomPoint X=181.97 Y=-105 Z=0
    g10: Circle CenterX=6 CenterY=-6 CenterZ=0 NormalX=0 NormalY=0 NormalZ=1 AngleXU=0 Radius=1.75
    g11: Circle CenterX=175.97 CenterY=-6 CenterZ=0 NormalX=0 NormalY=0 NormalZ=1 AngleXU=0 Radius=1.75
    g12: Circle CenterX=6 CenterY=-99 CenterZ=0 NormalX=0 NormalY=0 NormalZ=1 AngleXU=0 Radius=1.75
    g13: Circle CenterX=175.97 CenterY=-99 CenterZ=0 NormalX=0 NormalY=0 NormalZ=1 AngleXU=0 Radius=1.75
    g14: LineSegment StartX=6 StartY=-6 StartZ=0 EndX=175.97 EndY=-6 EndZ=0
    g15: LineSegment StartX=175.97 StartY=-6 StartZ=0 EndX=175.97 EndY=-99 EndZ=0
    g16: LineSegment StartX=175.97 StartY=-99 StartZ=0 EndX=6 EndY=-99 EndZ=0
    g17: LineSegment StartX=6 StartY=-99 StartZ=0 EndX=6 EndY=-6 EndZ=0
  constraints (43):
    c: Tangent(g0,g1) = 1.5708
    c: Tangent(g1,g2) = 1.5708
    c: Tangent(g2,g3) = 1.5708
    c: Tangent(g3,g4) = 1.5708
    c: Tangent(g4,g5) = 1.5708
    c: Tangent(g5,g6) = 1.5708
    c: Tangent(g6,g7) = 1.5708
    c: Tangent(g7,g0) = 1.5708
    c: Horizontal(g1)
    c: Horizontal(g5)
    c: Vertical(g3)
    c: Vertical(g7)
    c: Equal(g0,g2)
    c: Equal(g2,g4)
    c: Equal(g4,g6)
    c: PointOnObject(g8,g1)
    c: PointOnObject(g8,g7)
    c: PointOnObject(g9,g3)
    c: PointOnObject(g9,g5)
    c: Coincident(g8,g-1)
    c: Diameter(g0) = 8
    c: DistanceX(g8,g2) = 181.97
    c: DistanceY(g9,g1) = 105
    c: Coincident(g14,g15)
    c: Coincident(g15,g16)
    c: Coincident(g16,g17)
    c: Coincident(g17,g14)
    c: Horizontal(g14)
    c: Horizontal(g16)
    c: Vertical(g15)
    c: Vertical(g17)
    c: Coincident(g14,g10)
    c: Coincident(g15,g13)
    c: Coincident(g12,g16)
    c: Coincident(g11,g14)
    c: DistanceX(g0,g10) = 6
    c: DistanceY(g10,g0) = 6
    c: DistanceY(g4,g13) = 6
    c: DistanceX(g13,g3) = 6
    c: Equal(g10,g11)
    c: Equal(g11,g13)
    c: Equal(g13,g12)
    c: Diameter(g10) = 3.5
FEATURE [PartDesign::Pad] Pad006
  Direction = (0,0,1)
  Length = 4
  Length2 = 10
  Profile = -> Sketch012
  ReferenceAxis = -> Sketch012 [N_Axis]
  Type = 0
FEATURE [PartDesign::Chamfer] Chamfer001
  Angle = 45
  Base = -> Pad006 [Edge33,Edge30,Edge36,Edge27]
  BaseFeature = -> Pad006
  ChamferType = 0
  FlipDirection = false
  Size = 2
  Size2 = 1
  SupportTransform = false
  UseAllEdges = false
FEATURE [PartDesign::Body] Body003
  Group = -> [Sketch012,Pad006,Chamfer001]
  Origin = -> Origin005
  Tip = -> Chamfer001
FEATURE [App::Part] Part001
  Group = -> [Body003]
  Origin = -> Origin004
